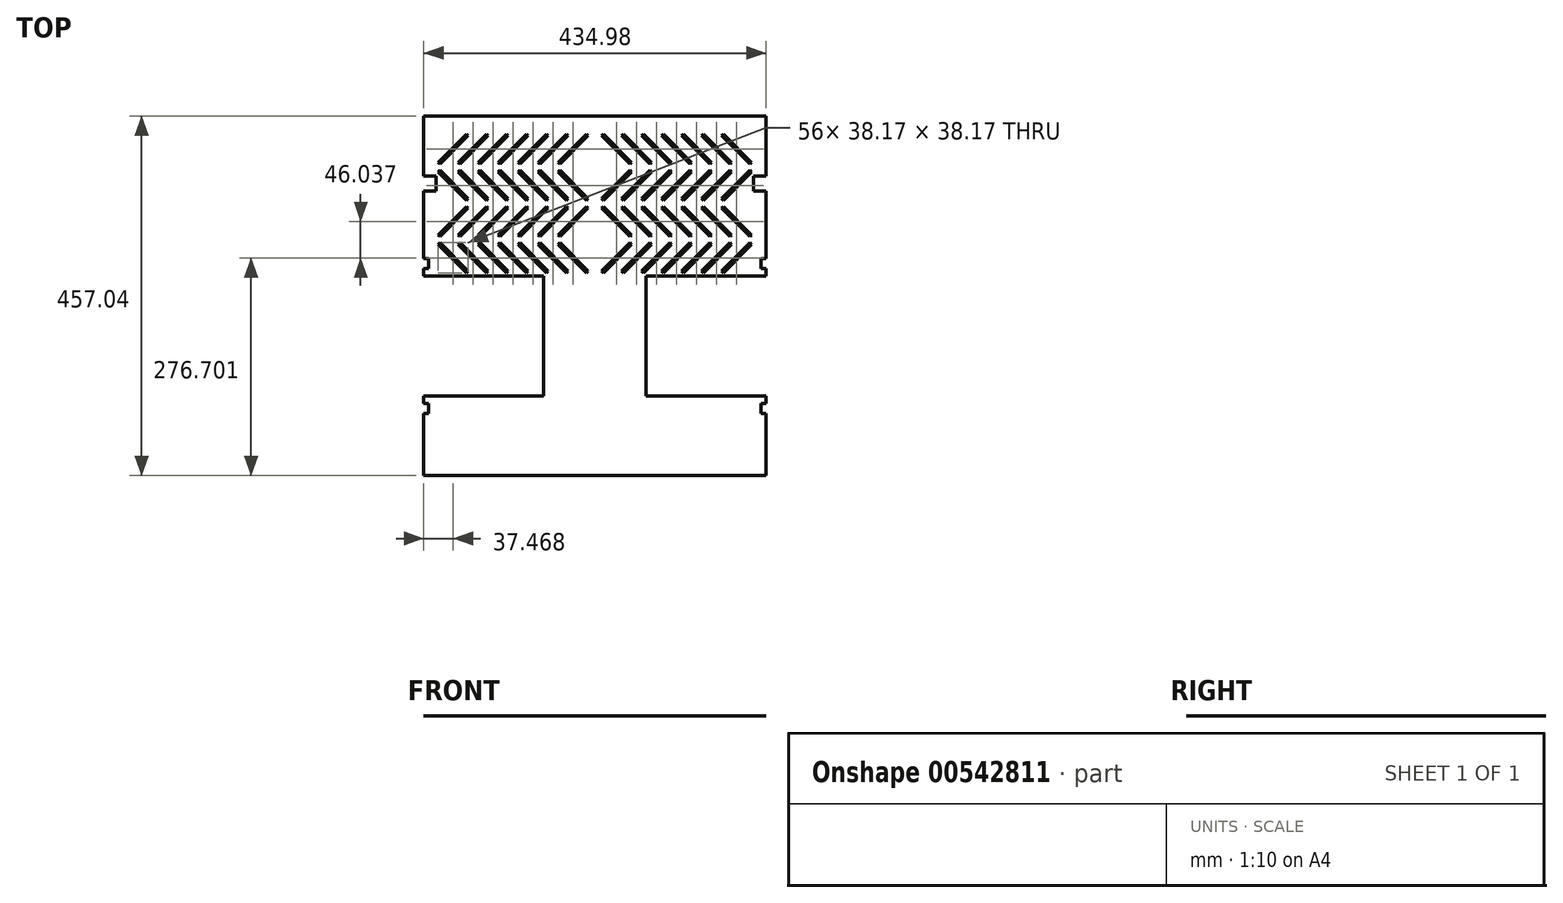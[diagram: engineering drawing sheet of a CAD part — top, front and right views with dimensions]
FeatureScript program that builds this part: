
annotation { "Feature Type Name" : "Feature", "Feature Type Description" : "" }
export const myFeature = defineFeature(function(context is Context, id is Id, definition is map)
    precondition{}
    {
        {
            var Q0;
            Q0=qCreatedBy(makeId("Top.planeOp"),FACE);
            var sketch = newSketch(context, id + "F0", { "sketchPlane" : qUnion([Q0])});
            skLineSegment(sketch, "E0", {"start": v(-217.49, -228.52) * mm, "end": v(-217.49, -149.3) * mm});
            skLineSegment(sketch, "E1", {"start": v(-217.49, -149.3) * mm, "end": v(-211.14, -149.3) * mm});
            skLineSegment(sketch, "E2", {"start": v(-211.14, -149.3) * mm, "end": v(-211.14, -136.6) * mm});
            skLineSegment(sketch, "E3", {"start": v(-211.14, -136.6) * mm, "end": v(-217.49, -136.6) * mm});
            skLineSegment(sketch, "E4", {"start": v(-217.49, -136.6) * mm, "end": v(-217.49, -127.08) * mm});
            skLineSegment(sketch, "E5", {"start": v(-217.49, -127.08) * mm, "end": v(-65.09, -127.08) * mm});
            skLineSegment(sketch, "E6", {"start": v(-65.09, -127.08) * mm, "end": v(-65.09, 25.32) * mm});
            skLineSegment(sketch, "E7", {"start": v(-65.09, 25.32) * mm, "end": v(-217.49, 25.32) * mm});
            skLineSegment(sketch, "E8", {"start": v(-217.49, 25.32) * mm, "end": v(-217.49, 34.85) * mm});
            skLineSegment(sketch, "E9", {"start": v(-217.49, 34.85) * mm, "end": v(-211.14, 34.85) * mm});
            skLineSegment(sketch, "E10", {"start": v(-211.14, 34.85) * mm, "end": v(-211.14, 47.55) * mm});
            skLineSegment(sketch, "E11", {"start": v(-211.14, 47.55) * mm, "end": v(-217.49, 47.55) * mm});
            skLineSegment(sketch, "E12", {"start": v(-217.49, 47.55) * mm, "end": v(-217.49, 133.27) * mm});
            skLineSegment(sketch, "E13", {"start": v(-217.49, 133.27) * mm, "end": v(-201.61, 133.27) * mm});
            skLineSegment(sketch, "E14", {"start": v(-201.61, 133.27) * mm, "end": v(-201.61, 152.32) * mm});
            skLineSegment(sketch, "E15", {"start": v(-201.61, 152.32) * mm, "end": v(-217.49, 152.32) * mm});
            skLineSegment(sketch, "E16", {"start": v(-217.49, 152.32) * mm, "end": v(-217.49, 228.52) * mm});
            skLineSegment(sketch, "E17", {"start": v(-217.49, 228.52) * mm, "end": v(217.49, 228.52) * mm});
            skLineSegment(sketch, "E18", {"start": v(217.49, 228.52) * mm, "end": v(217.49, 152.32) * mm});
            skLineSegment(sketch, "E19", {"start": v(217.49, 152.32) * mm, "end": v(201.61, 152.32) * mm});
            skLineSegment(sketch, "E20", {"start": v(201.61, 152.32) * mm, "end": v(201.61, 133.27) * mm});
            skLineSegment(sketch, "E21", {"start": v(201.61, 133.27) * mm, "end": v(217.49, 133.27) * mm});
            skLineSegment(sketch, "E22", {"start": v(217.49, 133.27) * mm, "end": v(217.49, 47.55) * mm});
            skLineSegment(sketch, "E23", {"start": v(217.49, 47.55) * mm, "end": v(211.14, 47.55) * mm});
            skLineSegment(sketch, "E24", {"start": v(211.14, 47.55) * mm, "end": v(211.14, 34.85) * mm});
            skLineSegment(sketch, "E25", {"start": v(211.14, 34.85) * mm, "end": v(217.49, 34.85) * mm});
            skLineSegment(sketch, "E26", {"start": v(217.49, 34.85) * mm, "end": v(217.49, 25.32) * mm});
            skLineSegment(sketch, "E27", {"start": v(217.49, 25.32) * mm, "end": v(65.09, 25.32) * mm});
            skLineSegment(sketch, "E28", {"start": v(65.09, 25.32) * mm, "end": v(65.09, -127.08) * mm});
            skLineSegment(sketch, "E29", {"start": v(65.09, -127.08) * mm, "end": v(217.49, -127.08) * mm});
            skLineSegment(sketch, "E30", {"start": v(217.49, -127.08) * mm, "end": v(217.49, -136.6) * mm});
            skLineSegment(sketch, "E31", {"start": v(217.49, -136.6) * mm, "end": v(211.14, -136.6) * mm});
            skLineSegment(sketch, "E32", {"start": v(211.14, -136.6) * mm, "end": v(211.14, -149.3) * mm});
            skLineSegment(sketch, "E33", {"start": v(211.14, -149.3) * mm, "end": v(217.49, -149.3) * mm});
            skLineSegment(sketch, "E34", {"start": v(217.49, -149.3) * mm, "end": v(217.49, -228.52) * mm});
            skLineSegment(sketch, "E35", {"start": v(217.49, -228.52) * mm, "end": v(-217.49, -228.52) * mm});
            skLineSegment(sketch, "E36", {"start": v(-196.86, 167.21) * mm, "end": v(-199.1, 169.46) * mm});
            skLineSegment(sketch, "E37", {"start": v(-199.1, 169.46) * mm, "end": v(-163.18, 205.38) * mm});
            skLineSegment(sketch, "E38", {"start": v(-163.18, 205.38) * mm, "end": v(-160.94, 203.13) * mm});
            skLineSegment(sketch, "E39", {"start": v(-160.94, 203.13) * mm, "end": v(-196.86, 167.21) * mm});
            skLineSegment(sketch, "E40", {"start": v(-171.46, 167.21) * mm, "end": v(-173.7, 169.46) * mm});
            skLineSegment(sketch, "E41", {"start": v(-173.7, 169.46) * mm, "end": v(-137.78, 205.38) * mm});
            skLineSegment(sketch, "E42", {"start": v(-137.78, 205.38) * mm, "end": v(-135.54, 203.13) * mm});
            skLineSegment(sketch, "E43", {"start": v(-135.54, 203.13) * mm, "end": v(-171.46, 167.21) * mm});
            skLineSegment(sketch, "E44", {"start": v(-146.06, 167.21) * mm, "end": v(-148.3, 169.46) * mm});
            skLineSegment(sketch, "E45", {"start": v(-148.3, 169.46) * mm, "end": v(-112.38, 205.38) * mm});
            skLineSegment(sketch, "E46", {"start": v(-112.38, 205.38) * mm, "end": v(-110.14, 203.13) * mm});
            skLineSegment(sketch, "E47", {"start": v(-110.14, 203.13) * mm, "end": v(-146.06, 167.21) * mm});
            skLineSegment(sketch, "E48", {"start": v(-120.66, 167.21) * mm, "end": v(-122.9, 169.46) * mm});
            skLineSegment(sketch, "E49", {"start": v(-122.9, 169.46) * mm, "end": v(-86.98, 205.38) * mm});
            skLineSegment(sketch, "E50", {"start": v(-86.98, 205.38) * mm, "end": v(-84.74, 203.13) * mm});
            skLineSegment(sketch, "E51", {"start": v(-84.74, 203.13) * mm, "end": v(-120.66, 167.21) * mm});
            skLineSegment(sketch, "E52", {"start": v(-95.26, 167.21) * mm, "end": v(-97.5, 169.46) * mm});
            skLineSegment(sketch, "E53", {"start": v(-97.5, 169.46) * mm, "end": v(-61.58, 205.38) * mm});
            skLineSegment(sketch, "E54", {"start": v(-61.58, 205.38) * mm, "end": v(-59.34, 203.13) * mm});
            skLineSegment(sketch, "E55", {"start": v(-59.34, 203.13) * mm, "end": v(-95.26, 167.21) * mm});
            skLineSegment(sketch, "E56", {"start": v(-69.86, 167.21) * mm, "end": v(-72.1, 169.46) * mm});
            skLineSegment(sketch, "E57", {"start": v(-72.1, 169.46) * mm, "end": v(-36.18, 205.38) * mm});
            skLineSegment(sketch, "E58", {"start": v(-36.18, 205.38) * mm, "end": v(-33.94, 203.13) * mm});
            skLineSegment(sketch, "E59", {"start": v(-33.94, 203.13) * mm, "end": v(-69.86, 167.21) * mm});
            skLineSegment(sketch, "E60", {"start": v(-44.46, 167.21) * mm, "end": v(-46.7, 169.46) * mm});
            skLineSegment(sketch, "E61", {"start": v(-46.7, 169.46) * mm, "end": v(-10.78, 205.38) * mm});
            skLineSegment(sketch, "E62", {"start": v(-10.78, 205.38) * mm, "end": v(-8.54, 203.13) * mm});
            skLineSegment(sketch, "E63", {"start": v(-8.54, 203.13) * mm, "end": v(-44.46, 167.21) * mm});
            skLineSegment(sketch, "E64", {"start": v(199.1, 169.46) * mm, "end": v(196.86, 167.21) * mm});
            skLineSegment(sketch, "E65", {"start": v(196.86, 167.21) * mm, "end": v(160.94, 203.13) * mm});
            skLineSegment(sketch, "E66", {"start": v(160.94, 203.13) * mm, "end": v(163.18, 205.38) * mm});
            skLineSegment(sketch, "E67", {"start": v(163.18, 205.38) * mm, "end": v(199.1, 169.46) * mm});
            skLineSegment(sketch, "E68", {"start": v(173.7, 169.46) * mm, "end": v(171.46, 167.21) * mm});
            skLineSegment(sketch, "E69", {"start": v(171.46, 167.21) * mm, "end": v(135.54, 203.13) * mm});
            skLineSegment(sketch, "E70", {"start": v(135.54, 203.13) * mm, "end": v(137.78, 205.38) * mm});
            skLineSegment(sketch, "E71", {"start": v(137.78, 205.38) * mm, "end": v(173.7, 169.46) * mm});
            skLineSegment(sketch, "E72", {"start": v(148.3, 169.46) * mm, "end": v(146.06, 167.21) * mm});
            skLineSegment(sketch, "E73", {"start": v(146.06, 167.21) * mm, "end": v(110.14, 203.13) * mm});
            skLineSegment(sketch, "E74", {"start": v(110.14, 203.13) * mm, "end": v(112.38, 205.38) * mm});
            skLineSegment(sketch, "E75", {"start": v(112.38, 205.38) * mm, "end": v(148.3, 169.46) * mm});
            skLineSegment(sketch, "E76", {"start": v(122.9, 169.46) * mm, "end": v(120.66, 167.21) * mm});
            skLineSegment(sketch, "E77", {"start": v(120.66, 167.21) * mm, "end": v(84.74, 203.13) * mm});
            skLineSegment(sketch, "E78", {"start": v(84.74, 203.13) * mm, "end": v(86.98, 205.38) * mm});
            skLineSegment(sketch, "E79", {"start": v(86.98, 205.38) * mm, "end": v(122.9, 169.46) * mm});
            skLineSegment(sketch, "E80", {"start": v(97.5, 169.46) * mm, "end": v(95.26, 167.21) * mm});
            skLineSegment(sketch, "E81", {"start": v(95.26, 167.21) * mm, "end": v(59.34, 203.13) * mm});
            skLineSegment(sketch, "E82", {"start": v(59.34, 203.13) * mm, "end": v(61.58, 205.38) * mm});
            skLineSegment(sketch, "E83", {"start": v(61.58, 205.38) * mm, "end": v(97.5, 169.46) * mm});
            skLineSegment(sketch, "E84", {"start": v(72.1, 169.46) * mm, "end": v(69.86, 167.21) * mm});
            skLineSegment(sketch, "E85", {"start": v(69.86, 167.21) * mm, "end": v(33.94, 203.13) * mm});
            skLineSegment(sketch, "E86", {"start": v(33.94, 203.13) * mm, "end": v(36.18, 205.38) * mm});
            skLineSegment(sketch, "E87", {"start": v(36.18, 205.38) * mm, "end": v(72.1, 169.46) * mm});
            skLineSegment(sketch, "E88", {"start": v(46.7, 169.46) * mm, "end": v(44.46, 167.21) * mm});
            skLineSegment(sketch, "E89", {"start": v(44.46, 167.21) * mm, "end": v(8.54, 203.13) * mm});
            skLineSegment(sketch, "E90", {"start": v(8.54, 203.13) * mm, "end": v(10.78, 205.38) * mm});
            skLineSegment(sketch, "E91", {"start": v(10.78, 205.38) * mm, "end": v(46.7, 169.46) * mm});
            skLineSegment(sketch, "E92", {"start": v(-196.86, 75.14) * mm, "end": v(-199.1, 77.38) * mm});
            skLineSegment(sketch, "E93", {"start": v(-199.1, 77.38) * mm, "end": v(-163.18, 113.3) * mm});
            skLineSegment(sketch, "E94", {"start": v(-163.18, 113.3) * mm, "end": v(-160.94, 111.06) * mm});
            skLineSegment(sketch, "E95", {"start": v(-160.94, 111.06) * mm, "end": v(-196.86, 75.14) * mm});
            skLineSegment(sketch, "E96", {"start": v(-171.46, 75.14) * mm, "end": v(-173.7, 77.38) * mm});
            skLineSegment(sketch, "E97", {"start": v(-173.7, 77.38) * mm, "end": v(-137.78, 113.3) * mm});
            skLineSegment(sketch, "E98", {"start": v(-137.78, 113.3) * mm, "end": v(-135.54, 111.06) * mm});
            skLineSegment(sketch, "E99", {"start": v(-135.54, 111.06) * mm, "end": v(-171.46, 75.14) * mm});
            skLineSegment(sketch, "E100", {"start": v(-146.06, 75.14) * mm, "end": v(-148.3, 77.38) * mm});
            skLineSegment(sketch, "E101", {"start": v(-148.3, 77.38) * mm, "end": v(-112.38, 113.3) * mm});
            skLineSegment(sketch, "E102", {"start": v(-112.38, 113.3) * mm, "end": v(-110.14, 111.06) * mm});
            skLineSegment(sketch, "E103", {"start": v(-110.14, 111.06) * mm, "end": v(-146.06, 75.14) * mm});
            skLineSegment(sketch, "E104", {"start": v(-120.66, 75.14) * mm, "end": v(-122.9, 77.38) * mm});
            skLineSegment(sketch, "E105", {"start": v(-122.9, 77.38) * mm, "end": v(-86.98, 113.3) * mm});
            skLineSegment(sketch, "E106", {"start": v(-86.98, 113.3) * mm, "end": v(-84.74, 111.06) * mm});
            skLineSegment(sketch, "E107", {"start": v(-84.74, 111.06) * mm, "end": v(-120.66, 75.14) * mm});
            skLineSegment(sketch, "E108", {"start": v(-95.26, 75.14) * mm, "end": v(-97.5, 77.38) * mm});
            skLineSegment(sketch, "E109", {"start": v(-97.5, 77.38) * mm, "end": v(-61.58, 113.3) * mm});
            skLineSegment(sketch, "E110", {"start": v(-61.58, 113.3) * mm, "end": v(-59.34, 111.06) * mm});
            skLineSegment(sketch, "E111", {"start": v(-59.34, 111.06) * mm, "end": v(-95.26, 75.14) * mm});
            skLineSegment(sketch, "E112", {"start": v(-69.86, 75.14) * mm, "end": v(-72.1, 77.38) * mm});
            skLineSegment(sketch, "E113", {"start": v(-72.1, 77.38) * mm, "end": v(-36.18, 113.3) * mm});
            skLineSegment(sketch, "E114", {"start": v(-36.18, 113.3) * mm, "end": v(-33.94, 111.06) * mm});
            skLineSegment(sketch, "E115", {"start": v(-33.94, 111.06) * mm, "end": v(-69.86, 75.14) * mm});
            skLineSegment(sketch, "E116", {"start": v(-44.46, 75.14) * mm, "end": v(-46.7, 77.38) * mm});
            skLineSegment(sketch, "E117", {"start": v(-46.7, 77.38) * mm, "end": v(-10.78, 113.3) * mm});
            skLineSegment(sketch, "E118", {"start": v(-10.78, 113.3) * mm, "end": v(-8.54, 111.06) * mm});
            skLineSegment(sketch, "E119", {"start": v(-8.54, 111.06) * mm, "end": v(-44.46, 75.14) * mm});
            skLineSegment(sketch, "E120", {"start": v(199.1, 77.38) * mm, "end": v(196.86, 75.14) * mm});
            skLineSegment(sketch, "E121", {"start": v(196.86, 75.14) * mm, "end": v(160.94, 111.06) * mm});
            skLineSegment(sketch, "E122", {"start": v(160.94, 111.06) * mm, "end": v(163.18, 113.3) * mm});
            skLineSegment(sketch, "E123", {"start": v(163.18, 113.3) * mm, "end": v(199.1, 77.38) * mm});
            skLineSegment(sketch, "E124", {"start": v(173.7, 77.38) * mm, "end": v(171.46, 75.14) * mm});
            skLineSegment(sketch, "E125", {"start": v(171.46, 75.14) * mm, "end": v(135.54, 111.06) * mm});
            skLineSegment(sketch, "E126", {"start": v(135.54, 111.06) * mm, "end": v(137.78, 113.3) * mm});
            skLineSegment(sketch, "E127", {"start": v(137.78, 113.3) * mm, "end": v(173.7, 77.38) * mm});
            skLineSegment(sketch, "E128", {"start": v(148.3, 77.38) * mm, "end": v(146.06, 75.14) * mm});
            skLineSegment(sketch, "E129", {"start": v(146.06, 75.14) * mm, "end": v(110.14, 111.06) * mm});
            skLineSegment(sketch, "E130", {"start": v(110.14, 111.06) * mm, "end": v(112.38, 113.3) * mm});
            skLineSegment(sketch, "E131", {"start": v(112.38, 113.3) * mm, "end": v(148.3, 77.38) * mm});
            skLineSegment(sketch, "E132", {"start": v(122.9, 77.38) * mm, "end": v(120.66, 75.14) * mm});
            skLineSegment(sketch, "E133", {"start": v(120.66, 75.14) * mm, "end": v(84.74, 111.06) * mm});
            skLineSegment(sketch, "E134", {"start": v(84.74, 111.06) * mm, "end": v(86.98, 113.3) * mm});
            skLineSegment(sketch, "E135", {"start": v(86.98, 113.3) * mm, "end": v(122.9, 77.38) * mm});
            skLineSegment(sketch, "E136", {"start": v(97.5, 77.38) * mm, "end": v(95.26, 75.14) * mm});
            skLineSegment(sketch, "E137", {"start": v(95.26, 75.14) * mm, "end": v(59.34, 111.06) * mm});
            skLineSegment(sketch, "E138", {"start": v(59.34, 111.06) * mm, "end": v(61.58, 113.3) * mm});
            skLineSegment(sketch, "E139", {"start": v(61.58, 113.3) * mm, "end": v(97.5, 77.38) * mm});
            skLineSegment(sketch, "E140", {"start": v(72.1, 77.38) * mm, "end": v(69.86, 75.14) * mm});
            skLineSegment(sketch, "E141", {"start": v(69.86, 75.14) * mm, "end": v(33.94, 111.06) * mm});
            skLineSegment(sketch, "E142", {"start": v(33.94, 111.06) * mm, "end": v(36.18, 113.3) * mm});
            skLineSegment(sketch, "E143", {"start": v(36.18, 113.3) * mm, "end": v(72.1, 77.38) * mm});
            skLineSegment(sketch, "E144", {"start": v(46.7, 77.38) * mm, "end": v(44.46, 75.14) * mm});
            skLineSegment(sketch, "E145", {"start": v(44.46, 75.14) * mm, "end": v(8.54, 111.06) * mm});
            skLineSegment(sketch, "E146", {"start": v(8.54, 111.06) * mm, "end": v(10.78, 113.3) * mm});
            skLineSegment(sketch, "E147", {"start": v(10.78, 113.3) * mm, "end": v(46.7, 77.38) * mm});
            skLineSegment(sketch, "E148", {"start": v(-196.86, 159.34) * mm, "end": v(-199.1, 157.1) * mm});
            skLineSegment(sketch, "E149", {"start": v(-199.1, 157.1) * mm, "end": v(-163.18, 121.17) * mm});
            skLineSegment(sketch, "E150", {"start": v(-163.18, 121.17) * mm, "end": v(-160.94, 123.42) * mm});
            skLineSegment(sketch, "E151", {"start": v(-160.94, 123.42) * mm, "end": v(-196.86, 159.34) * mm});
            skLineSegment(sketch, "E152", {"start": v(-171.46, 159.34) * mm, "end": v(-173.7, 157.1) * mm});
            skLineSegment(sketch, "E153", {"start": v(-173.7, 157.1) * mm, "end": v(-137.78, 121.17) * mm});
            skLineSegment(sketch, "E154", {"start": v(-137.78, 121.17) * mm, "end": v(-135.54, 123.42) * mm});
            skLineSegment(sketch, "E155", {"start": v(-135.54, 123.42) * mm, "end": v(-171.46, 159.34) * mm});
            skLineSegment(sketch, "E156", {"start": v(-146.06, 159.34) * mm, "end": v(-148.3, 157.1) * mm});
            skLineSegment(sketch, "E157", {"start": v(-148.3, 157.1) * mm, "end": v(-112.38, 121.17) * mm});
            skLineSegment(sketch, "E158", {"start": v(-112.38, 121.17) * mm, "end": v(-110.14, 123.42) * mm});
            skLineSegment(sketch, "E159", {"start": v(-110.14, 123.42) * mm, "end": v(-146.06, 159.34) * mm});
            skLineSegment(sketch, "E160", {"start": v(-120.66, 159.34) * mm, "end": v(-122.9, 157.1) * mm});
            skLineSegment(sketch, "E161", {"start": v(-122.9, 157.1) * mm, "end": v(-86.98, 121.17) * mm});
            skLineSegment(sketch, "E162", {"start": v(-86.98, 121.17) * mm, "end": v(-84.74, 123.42) * mm});
            skLineSegment(sketch, "E163", {"start": v(-84.74, 123.42) * mm, "end": v(-120.66, 159.34) * mm});
            skLineSegment(sketch, "E164", {"start": v(-95.26, 159.34) * mm, "end": v(-97.5, 157.1) * mm});
            skLineSegment(sketch, "E165", {"start": v(-97.5, 157.1) * mm, "end": v(-61.58, 121.17) * mm});
            skLineSegment(sketch, "E166", {"start": v(-61.58, 121.17) * mm, "end": v(-59.34, 123.42) * mm});
            skLineSegment(sketch, "E167", {"start": v(-59.34, 123.42) * mm, "end": v(-95.26, 159.34) * mm});
            skLineSegment(sketch, "E168", {"start": v(-69.86, 159.34) * mm, "end": v(-72.1, 157.1) * mm});
            skLineSegment(sketch, "E169", {"start": v(-72.1, 157.1) * mm, "end": v(-36.18, 121.17) * mm});
            skLineSegment(sketch, "E170", {"start": v(-36.18, 121.17) * mm, "end": v(-33.94, 123.42) * mm});
            skLineSegment(sketch, "E171", {"start": v(-33.94, 123.42) * mm, "end": v(-69.86, 159.34) * mm});
            skLineSegment(sketch, "E172", {"start": v(-44.46, 159.34) * mm, "end": v(-46.7, 157.1) * mm});
            skLineSegment(sketch, "E173", {"start": v(-46.7, 157.1) * mm, "end": v(-10.78, 121.17) * mm});
            skLineSegment(sketch, "E174", {"start": v(-10.78, 121.17) * mm, "end": v(-8.54, 123.42) * mm});
            skLineSegment(sketch, "E175", {"start": v(-8.54, 123.42) * mm, "end": v(-44.46, 159.34) * mm});
            skLineSegment(sketch, "E176", {"start": v(199.1, 157.1) * mm, "end": v(196.86, 159.34) * mm});
            skLineSegment(sketch, "E177", {"start": v(196.86, 159.34) * mm, "end": v(160.94, 123.42) * mm});
            skLineSegment(sketch, "E178", {"start": v(160.94, 123.42) * mm, "end": v(163.18, 121.17) * mm});
            skLineSegment(sketch, "E179", {"start": v(163.18, 121.17) * mm, "end": v(199.1, 157.1) * mm});
            skLineSegment(sketch, "E180", {"start": v(173.7, 157.1) * mm, "end": v(171.46, 159.34) * mm});
            skLineSegment(sketch, "E181", {"start": v(171.46, 159.34) * mm, "end": v(135.54, 123.42) * mm});
            skLineSegment(sketch, "E182", {"start": v(135.54, 123.42) * mm, "end": v(137.78, 121.17) * mm});
            skLineSegment(sketch, "E183", {"start": v(137.78, 121.17) * mm, "end": v(173.7, 157.1) * mm});
            skLineSegment(sketch, "E184", {"start": v(148.3, 157.1) * mm, "end": v(146.06, 159.34) * mm});
            skLineSegment(sketch, "E185", {"start": v(146.06, 159.34) * mm, "end": v(110.14, 123.42) * mm});
            skLineSegment(sketch, "E186", {"start": v(110.14, 123.42) * mm, "end": v(112.38, 121.17) * mm});
            skLineSegment(sketch, "E187", {"start": v(112.38, 121.17) * mm, "end": v(148.3, 157.1) * mm});
            skLineSegment(sketch, "E188", {"start": v(122.9, 157.1) * mm, "end": v(120.66, 159.34) * mm});
            skLineSegment(sketch, "E189", {"start": v(120.66, 159.34) * mm, "end": v(84.74, 123.42) * mm});
            skLineSegment(sketch, "E190", {"start": v(84.74, 123.42) * mm, "end": v(86.98, 121.17) * mm});
            skLineSegment(sketch, "E191", {"start": v(86.98, 121.17) * mm, "end": v(122.9, 157.1) * mm});
            skLineSegment(sketch, "E192", {"start": v(97.5, 157.1) * mm, "end": v(95.26, 159.34) * mm});
            skLineSegment(sketch, "E193", {"start": v(95.26, 159.34) * mm, "end": v(59.34, 123.42) * mm});
            skLineSegment(sketch, "E194", {"start": v(59.34, 123.42) * mm, "end": v(61.58, 121.17) * mm});
            skLineSegment(sketch, "E195", {"start": v(61.58, 121.17) * mm, "end": v(97.5, 157.1) * mm});
            skLineSegment(sketch, "E196", {"start": v(72.1, 157.1) * mm, "end": v(69.86, 159.34) * mm});
            skLineSegment(sketch, "E197", {"start": v(69.86, 159.34) * mm, "end": v(33.94, 123.42) * mm});
            skLineSegment(sketch, "E198", {"start": v(33.94, 123.42) * mm, "end": v(36.18, 121.17) * mm});
            skLineSegment(sketch, "E199", {"start": v(36.18, 121.17) * mm, "end": v(72.1, 157.1) * mm});
            skLineSegment(sketch, "E200", {"start": v(46.7, 157.1) * mm, "end": v(44.46, 159.34) * mm});
            skLineSegment(sketch, "E201", {"start": v(44.46, 159.34) * mm, "end": v(8.54, 123.42) * mm});
            skLineSegment(sketch, "E202", {"start": v(8.54, 123.42) * mm, "end": v(10.78, 121.17) * mm});
            skLineSegment(sketch, "E203", {"start": v(10.78, 121.17) * mm, "end": v(46.7, 157.1) * mm});
            skLineSegment(sketch, "E204", {"start": v(-196.86, 67.26) * mm, "end": v(-199.1, 65.02) * mm});
            skLineSegment(sketch, "E205", {"start": v(-199.1, 65.02) * mm, "end": v(-163.18, 29.1) * mm});
            skLineSegment(sketch, "E206", {"start": v(-163.18, 29.1) * mm, "end": v(-160.94, 31.34) * mm});
            skLineSegment(sketch, "E207", {"start": v(-160.94, 31.34) * mm, "end": v(-196.86, 67.26) * mm});
            skLineSegment(sketch, "E208", {"start": v(-171.46, 67.26) * mm, "end": v(-173.7, 65.02) * mm});
            skLineSegment(sketch, "E209", {"start": v(-173.7, 65.02) * mm, "end": v(-137.78, 29.1) * mm});
            skLineSegment(sketch, "E210", {"start": v(-137.78, 29.1) * mm, "end": v(-135.54, 31.34) * mm});
            skLineSegment(sketch, "E211", {"start": v(-135.54, 31.34) * mm, "end": v(-171.46, 67.26) * mm});
            skLineSegment(sketch, "E212", {"start": v(-146.06, 67.26) * mm, "end": v(-148.3, 65.02) * mm});
            skLineSegment(sketch, "E213", {"start": v(-148.3, 65.02) * mm, "end": v(-112.38, 29.1) * mm});
            skLineSegment(sketch, "E214", {"start": v(-112.38, 29.1) * mm, "end": v(-110.14, 31.34) * mm});
            skLineSegment(sketch, "E215", {"start": v(-110.14, 31.34) * mm, "end": v(-146.06, 67.26) * mm});
            skLineSegment(sketch, "E216", {"start": v(-120.66, 67.26) * mm, "end": v(-122.9, 65.02) * mm});
            skLineSegment(sketch, "E217", {"start": v(-122.9, 65.02) * mm, "end": v(-86.98, 29.1) * mm});
            skLineSegment(sketch, "E218", {"start": v(-86.98, 29.1) * mm, "end": v(-84.74, 31.34) * mm});
            skLineSegment(sketch, "E219", {"start": v(-84.74, 31.34) * mm, "end": v(-120.66, 67.26) * mm});
            skLineSegment(sketch, "E220", {"start": v(-95.26, 67.26) * mm, "end": v(-97.5, 65.02) * mm});
            skLineSegment(sketch, "E221", {"start": v(-97.5, 65.02) * mm, "end": v(-61.58, 29.1) * mm});
            skLineSegment(sketch, "E222", {"start": v(-61.58, 29.1) * mm, "end": v(-59.34, 31.34) * mm});
            skLineSegment(sketch, "E223", {"start": v(-59.34, 31.34) * mm, "end": v(-95.26, 67.26) * mm});
            skLineSegment(sketch, "E224", {"start": v(-69.86, 67.26) * mm, "end": v(-72.1, 65.02) * mm});
            skLineSegment(sketch, "E225", {"start": v(-72.1, 65.02) * mm, "end": v(-36.18, 29.1) * mm});
            skLineSegment(sketch, "E226", {"start": v(-36.18, 29.1) * mm, "end": v(-33.94, 31.34) * mm});
            skLineSegment(sketch, "E227", {"start": v(-33.94, 31.34) * mm, "end": v(-69.86, 67.26) * mm});
            skLineSegment(sketch, "E228", {"start": v(-44.46, 67.26) * mm, "end": v(-46.7, 65.02) * mm});
            skLineSegment(sketch, "E229", {"start": v(-46.7, 65.02) * mm, "end": v(-10.78, 29.1) * mm});
            skLineSegment(sketch, "E230", {"start": v(-10.78, 29.1) * mm, "end": v(-8.54, 31.34) * mm});
            skLineSegment(sketch, "E231", {"start": v(-8.54, 31.34) * mm, "end": v(-44.46, 67.26) * mm});
            skLineSegment(sketch, "E232", {"start": v(199.1, 65.02) * mm, "end": v(196.86, 67.26) * mm});
            skLineSegment(sketch, "E233", {"start": v(196.86, 67.26) * mm, "end": v(160.94, 31.34) * mm});
            skLineSegment(sketch, "E234", {"start": v(160.94, 31.34) * mm, "end": v(163.18, 29.1) * mm});
            skLineSegment(sketch, "E235", {"start": v(163.18, 29.1) * mm, "end": v(199.1, 65.02) * mm});
            skLineSegment(sketch, "E236", {"start": v(173.7, 65.02) * mm, "end": v(171.46, 67.26) * mm});
            skLineSegment(sketch, "E237", {"start": v(171.46, 67.26) * mm, "end": v(135.54, 31.34) * mm});
            skLineSegment(sketch, "E238", {"start": v(135.54, 31.34) * mm, "end": v(137.78, 29.1) * mm});
            skLineSegment(sketch, "E239", {"start": v(137.78, 29.1) * mm, "end": v(173.7, 65.02) * mm});
            skLineSegment(sketch, "E240", {"start": v(148.3, 65.02) * mm, "end": v(146.06, 67.26) * mm});
            skLineSegment(sketch, "E241", {"start": v(146.06, 67.26) * mm, "end": v(110.14, 31.34) * mm});
            skLineSegment(sketch, "E242", {"start": v(110.14, 31.34) * mm, "end": v(112.38, 29.1) * mm});
            skLineSegment(sketch, "E243", {"start": v(112.38, 29.1) * mm, "end": v(148.3, 65.02) * mm});
            skLineSegment(sketch, "E244", {"start": v(122.9, 65.02) * mm, "end": v(120.66, 67.26) * mm});
            skLineSegment(sketch, "E245", {"start": v(120.66, 67.26) * mm, "end": v(84.74, 31.34) * mm});
            skLineSegment(sketch, "E246", {"start": v(84.74, 31.34) * mm, "end": v(86.98, 29.1) * mm});
            skLineSegment(sketch, "E247", {"start": v(86.98, 29.1) * mm, "end": v(122.9, 65.02) * mm});
            skLineSegment(sketch, "E248", {"start": v(97.5, 65.02) * mm, "end": v(95.26, 67.26) * mm});
            skLineSegment(sketch, "E249", {"start": v(95.26, 67.26) * mm, "end": v(59.34, 31.34) * mm});
            skLineSegment(sketch, "E250", {"start": v(59.34, 31.34) * mm, "end": v(61.58, 29.1) * mm});
            skLineSegment(sketch, "E251", {"start": v(61.58, 29.1) * mm, "end": v(97.5, 65.02) * mm});
            skLineSegment(sketch, "E252", {"start": v(72.1, 65.02) * mm, "end": v(69.86, 67.26) * mm});
            skLineSegment(sketch, "E253", {"start": v(69.86, 67.26) * mm, "end": v(33.94, 31.34) * mm});
            skLineSegment(sketch, "E254", {"start": v(33.94, 31.34) * mm, "end": v(36.18, 29.1) * mm});
            skLineSegment(sketch, "E255", {"start": v(36.18, 29.1) * mm, "end": v(72.1, 65.02) * mm});
            skLineSegment(sketch, "E256", {"start": v(46.7, 65.02) * mm, "end": v(44.46, 67.26) * mm});
            skLineSegment(sketch, "E257", {"start": v(44.46, 67.26) * mm, "end": v(8.54, 31.34) * mm});
            skLineSegment(sketch, "E258", {"start": v(8.54, 31.34) * mm, "end": v(10.78, 29.1) * mm});
            skLineSegment(sketch, "E259", {"start": v(10.78, 29.1) * mm, "end": v(46.7, 65.02) * mm});
            skSolve(sketch);
        }
        {
            var Q0;
            Q0=makeQuery(id+"F0.imprint","IMPRINT",FACE,{"disambiguationData":[TD([[makeQuery(id+"F0.imprint","IMPRINT",EDGE,{"derivedFrom":sQuery(id+"F0.wireOp",EDGE,"E0")}),-1.0]])]});
            extrude(context, id + "F1", {"entities" : qUnion([Q0]), "depth" : 1 / 203.2 * mm});
        }
    });
